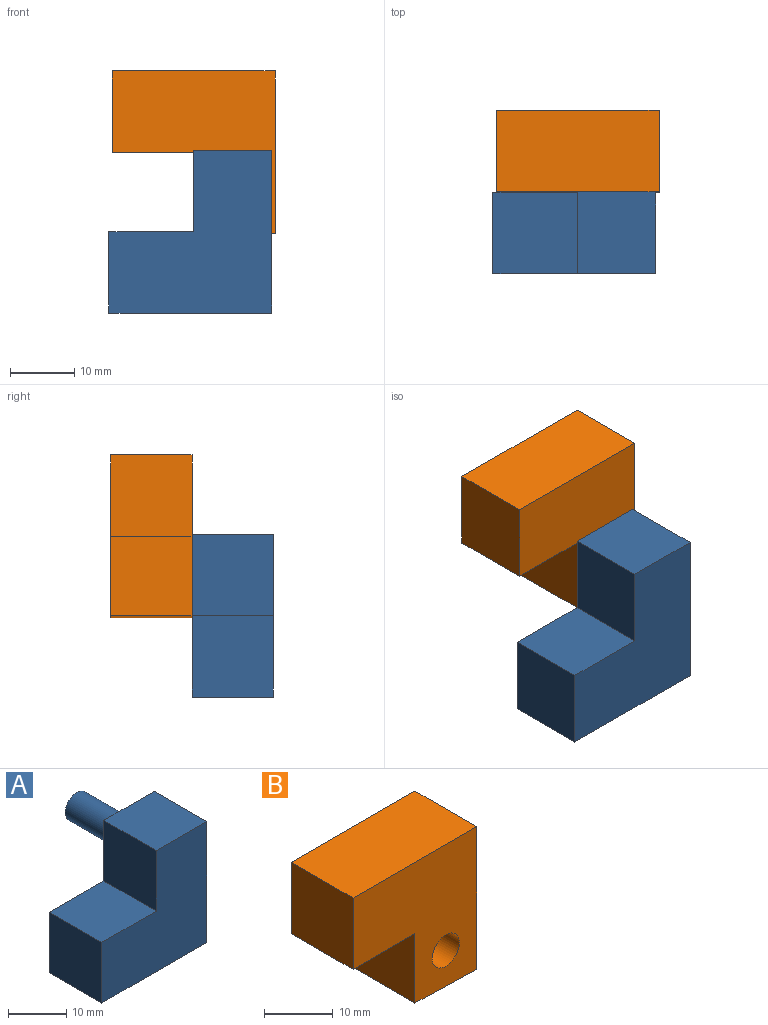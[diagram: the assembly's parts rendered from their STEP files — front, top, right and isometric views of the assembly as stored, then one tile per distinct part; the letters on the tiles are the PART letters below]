
ASSEMBLY  parts=2 mates=1
PART A: 10 faces, bbox 25.4x25.4x25.4 mm
  f0: plane 12.7x12.2mm, normal (0,0,1), area 154.9mm2, adj f1,f5,f6,f7
  f1: plane 12.7x12.7mm, normal (-1,0,0), area 161.3mm2, adj f0,f2,f6,f7
  f2: plane 13.2x12.7mm, normal (0,0,1), area 167.6mm2, adj f1,f3,f6,f7
  f3: plane 12.7x12.7mm, normal (-1,0,0), area 161.3mm2, adj f2,f4,f6,f7
  f4: plane 25.4x12.7mm, normal (0,0,-1), area 322.6mm2, adj f3,f5,f6,f7
  f5: plane 25.4x12.7mm, normal (1,0,0), area 322.6mm2, adj f0,f4,f6,f7
  f6: plane 25.4x25.4mm, normal (0,-1,0), area 477.5mm2, adj f0,f1,f2,f3,f4,f5
  f7: plane 25.4x25.4mm, normal (0,1,0), area 453mm2, adj f0,f1,f2,f3,f4,f5,f8
  f8: cylinder r=2.79mm len=12.7mm, axis (0,-1,0), area 223mm2, adj f7,f9
  f9: plane 5.59x5.59mm, normal (0,1,0), area 24.5mm2, adj f8
PART B: 9 faces, bbox 25.4x12.7x25.4 mm
  f0: plane 25.4x12.7mm, normal (0,0,1), area 322.6mm2, adj f1,f5,f7,f8
  f1: plane 12.7x12.7mm, normal (-1,0,0), area 161.3mm2, adj f0,f2,f7,f8
  f2: plane 12.71x12.7mm, normal (0,0,-1), area 161.4mm2, adj f1,f3,f7,f8
  f3: plane 12.7x12.34mm, normal (-1,0,0), area 156.7mm2, adj f2,f4,f7,f8
  f4: plane 12.7x12.7mm, normal (-0.03,0,-1), area 161.3mm2, adj f3,f5,f7,f8
  f5: plane 25.4x12.7mm, normal (1,0,0), area 322.6mm2, adj f0,f4,f7,f8
  f6: cylinder r=2.79mm len=12.7mm, axis (0,1,0), area 223mm2, adj f7,f8
  f7: plane 25.4x25.4mm, normal (0,-1,0), area 457mm2, adj f0,f1,f2,f3,f4,f5,f6
  f8: plane 25.4x25.4mm, normal (0,1,0), area 457mm2, adj f0,f1,f2,f3,f4,f5,f6
PLACE A t=(19.71,-0.66,21.36)mm
PLACE B t=(34.26,12.04,16.86)mm
MATE fastened B.f7 <-> A.f7  axis (0,-1,0) through (-36.14,-0.66,19.9)mm
